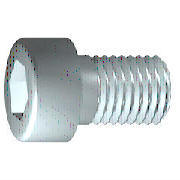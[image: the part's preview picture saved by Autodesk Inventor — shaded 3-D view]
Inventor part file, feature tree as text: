
AUTODESK INVENTOR PART (.ipt)
format: ipt  version: 2015 (Build 190159000, 159)  size: 185,344 bytes
history: native  units: mm (DEFAULTED — no unit token found)
features: sketch x2, extrude x1, plane x1, fillet x1
ambient origin geometry x7: Origin, YZ Plane, XY Plane, X Axis, Y Axis, Z Axis, Center Point
bodies: Solid1 (feature_tree), Body (feature_tree)
feature tree (5):
  extrude  "Slot"  Depth=5.0mm
  plane  "Work Plane1"
  fillet  "Fillet2"  Radius=5.0mm
  sketch  "Sketch1"  dims[d1=22.0mm d2=0.49086mm d3=5.0mm]
  sketch  "Sketch2"  dims[d4=2.5mm d5=60.0deg d6=5.0mm d7=5.0mm d8=4.618802mm d9=8.5mm d10=90.0deg d11=10.0mm d12=0.0mm d13=22.0mm d14=0.0mm d15=0.49076mm d16=0.49076mm d17=0.5mm d19=0.0mm d26=45.0mm d27=45.0deg d28=0.0mm d29=0.0mm d30=0.1mm]
